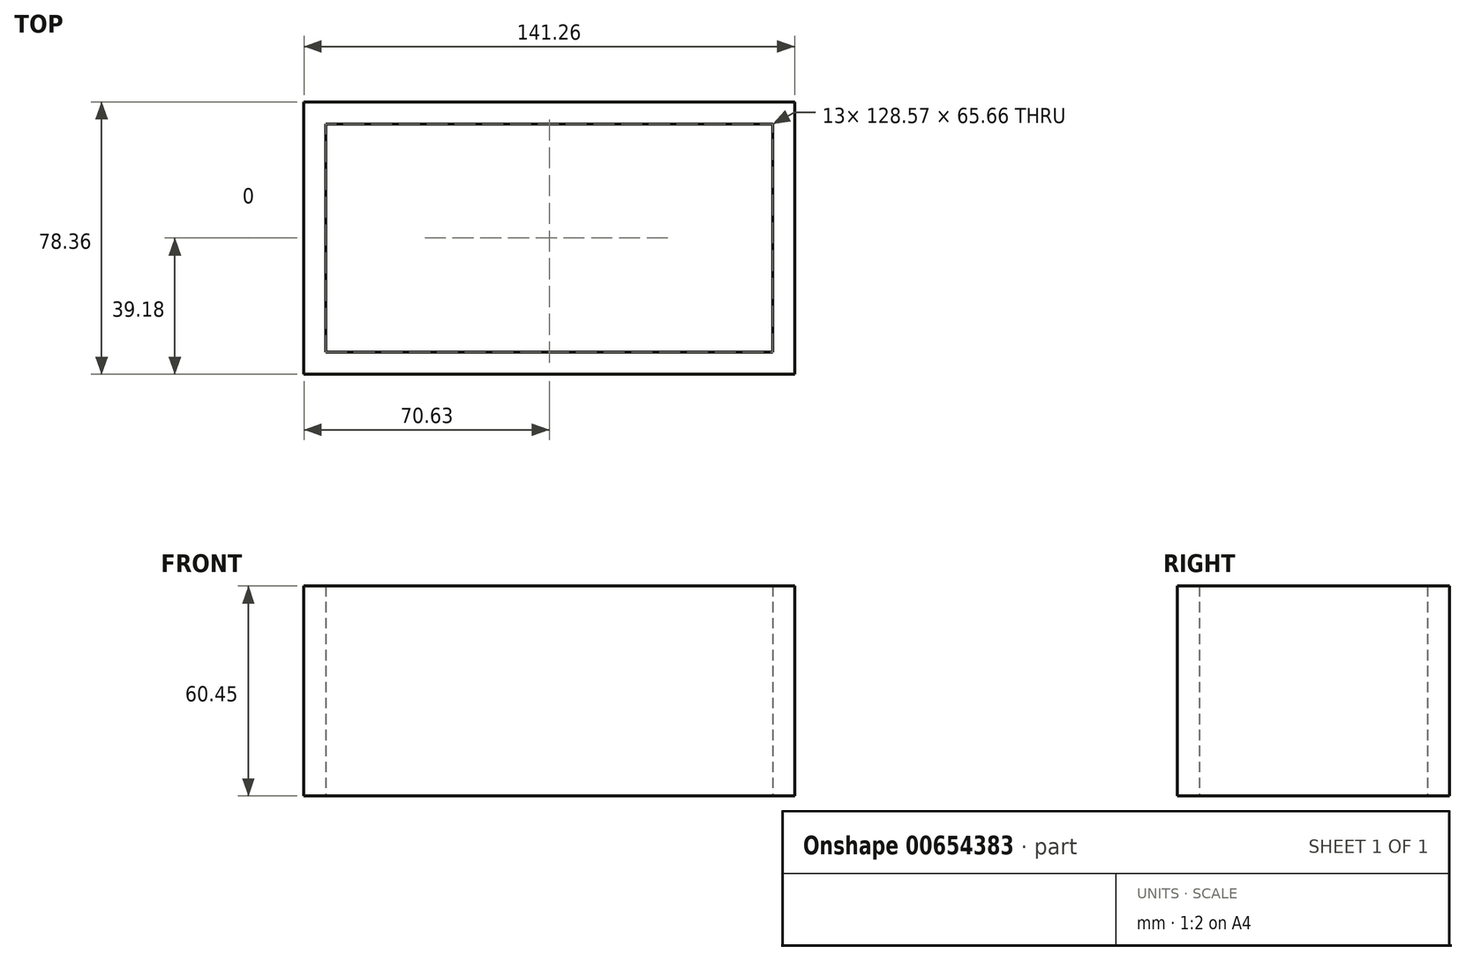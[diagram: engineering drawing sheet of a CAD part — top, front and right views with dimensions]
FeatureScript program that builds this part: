
annotation { "Feature Type Name" : "Feature", "Feature Type Description" : "" }
export const myFeature = defineFeature(function(context is Context, id is Id, definition is map)
    precondition{}
    {
        {
            var Q0;
            Q0=qCreatedBy(makeId("Top.planeOp"),FACE);
            var sketch = newSketch(context, id + "F0", { "sketchPlane" : qUnion([Q0])});
            skLineSegment(sketch, "E0.bottom", {"start": v(-64.28, 32.83) * mm, "end": v(64.28, 32.83) * mm});
            skLineSegment(sketch, "E0.top", {"start": v(-64.28, -32.83) * mm, "end": v(64.28, -32.83) * mm});
            skLineSegment(sketch, "E0.left", {"start": v(-64.28, 32.83) * mm, "end": v(-64.28, -32.83) * mm});
            skLineSegment(sketch, "E0.right", {"start": v(64.28, 32.83) * mm, "end": v(64.28, -32.83) * mm});
            skPoint(sketch, "E0.middle", {"position": v(0, 0) * mm});
            skLineSegment(sketch, "E1.0", {"start": v(-70.63, 39.18) * mm, "end": v(70.63, 39.18) * mm});
            skLineSegment(sketch, "E1.1", {"start": v(-70.63, 39.18) * mm, "end": v(-70.63, -39.18) * mm});
            skLineSegment(sketch, "E1.2", {"start": v(-70.63, -39.18) * mm, "end": v(70.63, -39.18) * mm});
            skLineSegment(sketch, "E1.3", {"start": v(70.63, 39.18) * mm, "end": v(70.63, -39.18) * mm});
            skSolve(sketch);
        }
        {
            var Q0;
            Q0=makeQuery(id+"F0.imprint","IMPRINT",FACE,{"disambiguationData":[TD([[makeQuery(id+"F0.imprint","IMPRINT",EDGE,{"derivedFrom":sQuery(id+"F0.wireOp",EDGE,"E0.bottom")}),1.0]])]});
            extrude(context, id + "F1", {"entities" : qUnion([Q0]), "depth" : 60.45 * mm, "offsetDistance" : 25.4 * mm});
        }
    });
